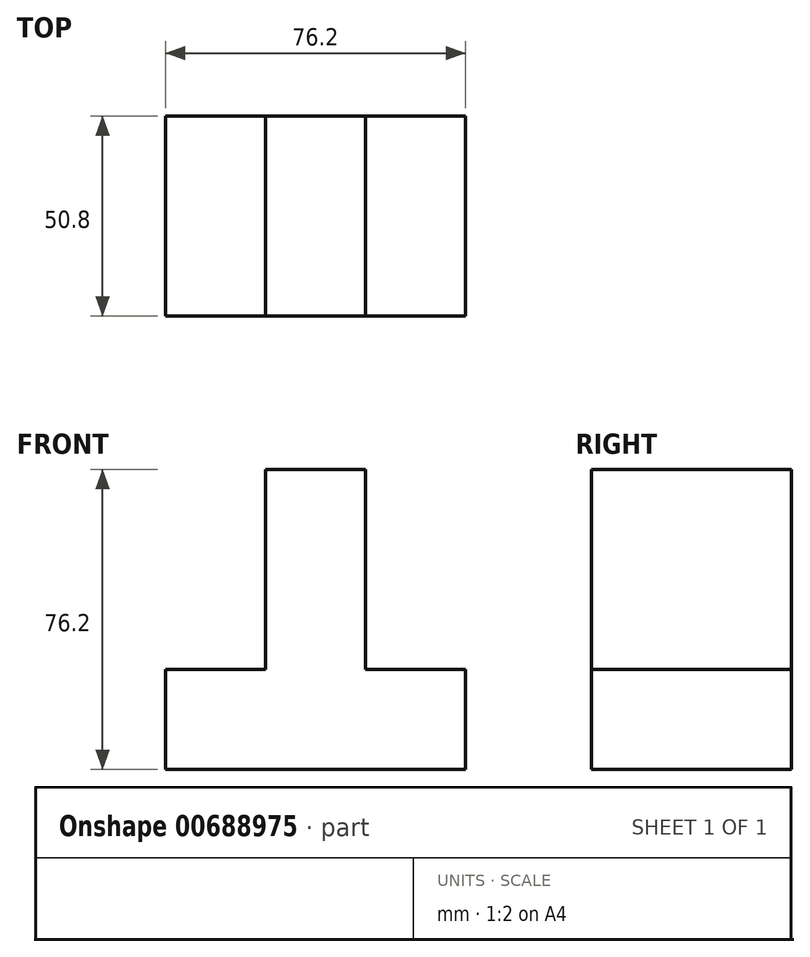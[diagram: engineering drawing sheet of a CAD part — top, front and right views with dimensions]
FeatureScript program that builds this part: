
annotation { "Feature Type Name" : "Feature", "Feature Type Description" : "" }
export const myFeature = defineFeature(function(context is Context, id is Id, definition is map)
    precondition{}
    {
        {
            var Q0;
            Q0=qCreatedBy(makeId("Front.planeOp"),FACE);
            var sketch = newSketch(context, id + "F0", { "sketchPlane" : qUnion([Q0])});
            skLineSegment(sketch, "E0", {"start": v(-49.93, -30.12) * mm, "end": v(26.27, -30.12) * mm});
            skLineSegment(sketch, "E1", {"start": v(26.27, -30.12) * mm, "end": v(26.27, -4.72) * mm});
            skLineSegment(sketch, "E2", {"start": v(26.27, -4.72) * mm, "end": v(0.87, -4.72) * mm});
            skLineSegment(sketch, "E3", {"start": v(0.87, -4.72) * mm, "end": v(0.87, 46.08) * mm});
            skLineSegment(sketch, "E4", {"start": v(0.87, 46.08) * mm, "end": v(-24.53, 46.08) * mm});
            skLineSegment(sketch, "E5", {"start": v(-24.53, 46.08) * mm, "end": v(-24.53, -4.72) * mm});
            skLineSegment(sketch, "E6", {"start": v(-24.53, -4.72) * mm, "end": v(-49.93, -4.72) * mm});
            skLineSegment(sketch, "E7", {"start": v(-49.93, -4.72) * mm, "end": v(-49.93, -30.12) * mm});
            skSolve(sketch);
        }
        {
            var Q0;
            Q0 = qSketchRegion(id + "F0", true);
            extrude(context, id + "F1", {"entities" : qUnion([Q0]), "depth" : 50.8 * mm, "offsetDistance" : 25.4 * mm});
        }
    });
